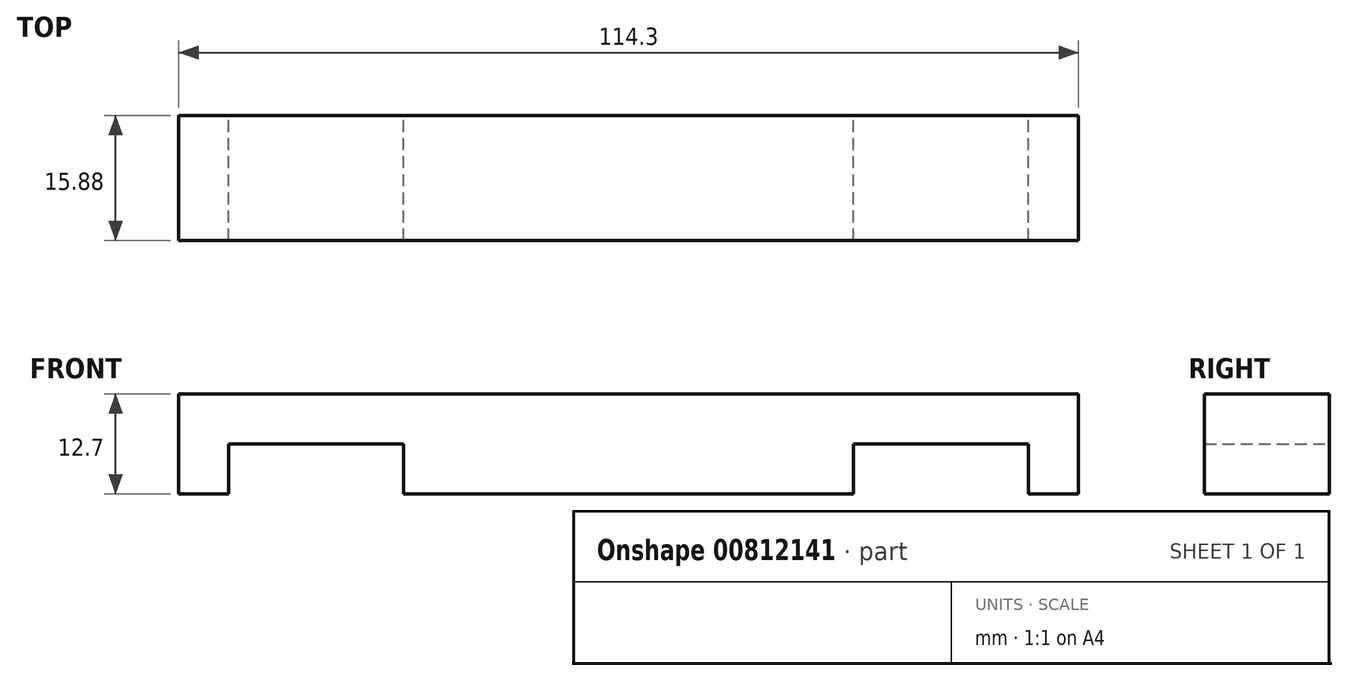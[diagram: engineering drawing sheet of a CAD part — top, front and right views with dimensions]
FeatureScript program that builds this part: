
annotation { "Feature Type Name" : "Feature", "Feature Type Description" : "" }
export const myFeature = defineFeature(function(context is Context, id is Id, definition is map)
    precondition{}
    {
        {
            var Q0;
            Q0=qCreatedBy(makeId("Front.planeOp"),FACE);
            var sketch = newSketch(context, id + "F0", { "sketchPlane" : qUnion([Q0])});
            skLineSegment(sketch, "E0", {"start": v(0, 0) * mm, "end": v(-57.15, 0) * mm});
            skLineSegment(sketch, "E1", {"start": v(-57.15, 0) * mm, "end": v(-57.15, -12.7) * mm});
            skLineSegment(sketch, "E2", {"start": v(-57.15, -12.7) * mm, "end": v(-50.8, -12.7) * mm});
            skLineSegment(sketch, "E3", {"start": v(-50.8, -12.7) * mm, "end": v(-50.8, -6.35) * mm});
            skLineSegment(sketch, "E4", {"start": v(-50.8, -6.35) * mm, "end": v(-28.58, -6.35) * mm});
            skLineSegment(sketch, "E5", {"start": v(-28.58, -6.35) * mm, "end": v(-28.58, -12.7) * mm});
            skLineSegment(sketch, "E6", {"start": v(-28.58, -12.7) * mm, "end": v(0, -12.7) * mm});
            skLineSegment(sketch, "E7.MirrorCS", {"start": v(50.8, -12.7) * mm, "end": v(50.8, -6.35) * mm});
            skLineSegment(sketch, "E8.MirrorCS", {"start": v(57.15, -12.7) * mm, "end": v(50.8, -12.7) * mm});
            skLineSegment(sketch, "E9.MirrorCS", {"start": v(50.8, -6.35) * mm, "end": v(28.58, -6.35) * mm});
            skLineSegment(sketch, "E10.MirrorCS", {"start": v(0, 0) * mm, "end": v(57.15, 0) * mm});
            skLineSegment(sketch, "E11.MirrorCS", {"start": v(57.15, 0) * mm, "end": v(57.15, -12.7) * mm});
            skLineSegment(sketch, "E12.MirrorCS", {"start": v(28.58, -6.35) * mm, "end": v(28.58, -12.7) * mm});
            skLineSegment(sketch, "E13.MirrorCS", {"start": v(28.58, -12.7) * mm, "end": v(0, -12.7) * mm});
            skSolve(sketch);
        }
        {
            var Q0;
            Q0=makeQuery(id+"F0.imprint","IMPRINT",FACE,{"disambiguationData":[TD([[makeQuery(id+"F0.imprint","IMPRINT",EDGE,{"derivedFrom":sQuery(id+"F0.wireOp",EDGE,"E0")}),1.0]])]});
            extrude(context, id + "F1", {"entities" : qUnion([Q0]), "depth" : 15.88 * mm, "offsetDistance" : 25.4 * mm});
        }
    });
